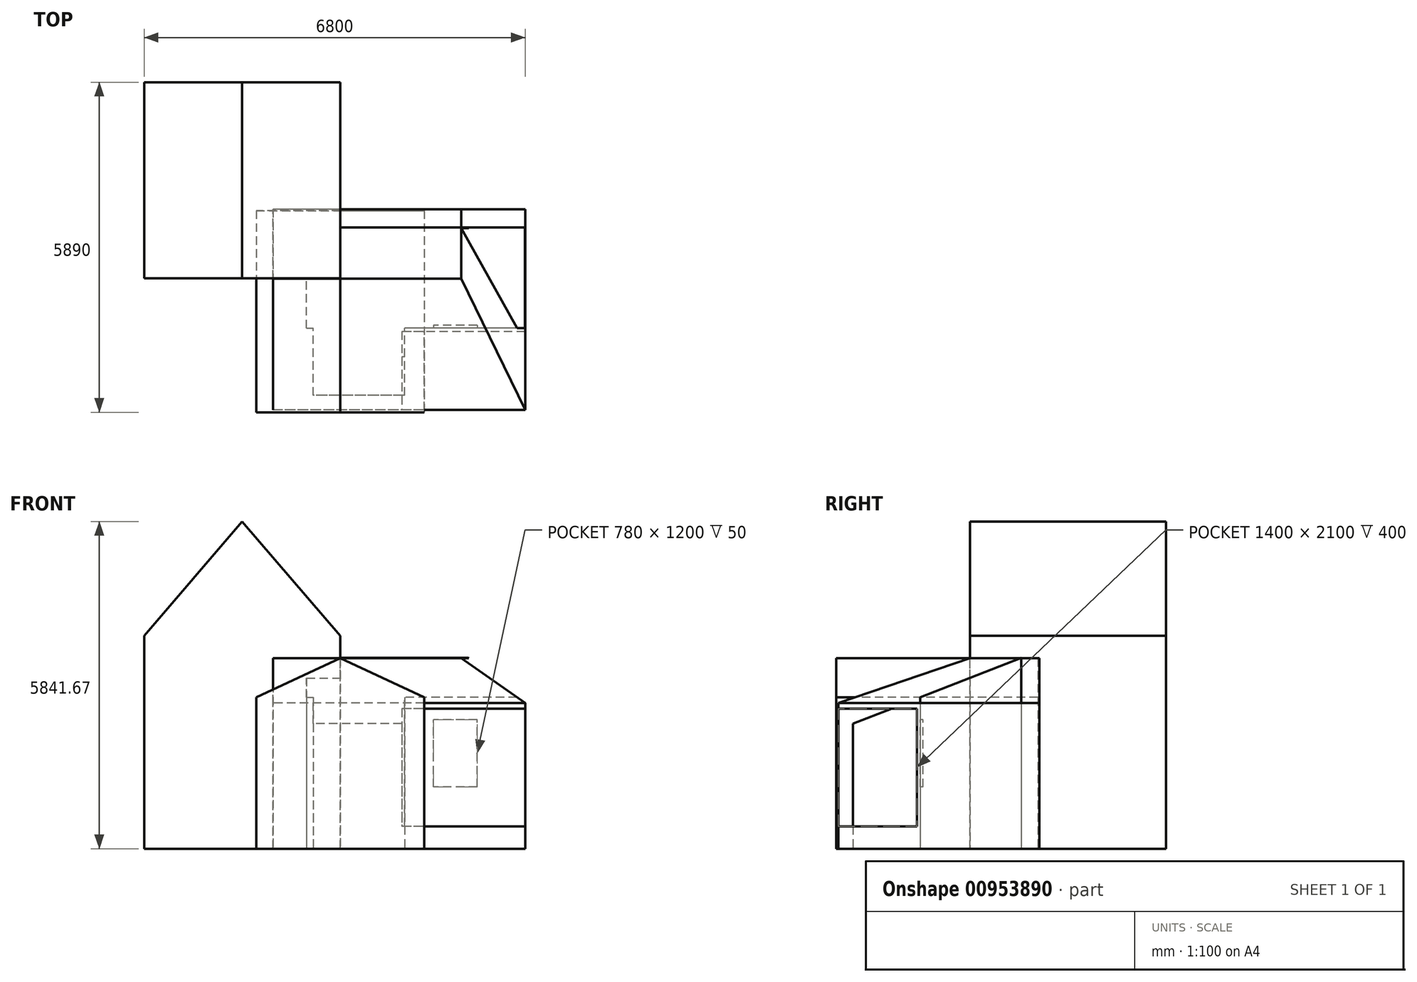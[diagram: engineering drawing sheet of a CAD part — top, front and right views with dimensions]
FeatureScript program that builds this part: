
annotation { "Feature Type Name" : "Feature", "Feature Type Description" : "" }
export const myFeature = defineFeature(function(context is Context, id is Id, definition is map)
    precondition{}
    {
        {
            var Q0;
            Q0=qCreatedBy(makeId("Right.planeOp"),FACE);
            var sketch = newSketch(context, id + "F0", { "sketchPlane" : qUnion([Q0])});
            skLineSegment(sketch, "E0", {"start": v(0, 0) * mm, "end": v(0, 2700) * mm});
            skLineSegment(sketch, "E1", {"start": v(1800, 0) * mm, "end": v(-1200, 0) * mm});
            skLineSegment(sketch, "E2", {"start": v(-1200, 0) * mm, "end": v(-1200, 2230) * mm});
            skLineSegment(sketch, "E3", {"start": v(-1200, 2230) * mm, "end": v(1800, 3405) * mm});
            skLineSegment(sketch, "E4", {"start": v(1800, 3405) * mm, "end": v(1800, 0) * mm});
            skSolve(sketch);
        }
        {
            var Q0;
            Q0 = qSketchRegion(id + "F0", true);
            extrude(context, id + "F1", {"entities" : qUnion([Q0]), "depth" : 3895 * mm, "offsetDistance" : 25 * mm});
        }
        {
            var Q0;
            Q0=qCreatedBy(makeId("Top.planeOp"),FACE);
            var sketch = newSketch(context, id + "F2", { "sketchPlane" : qUnion([Q0])});
            skLineSegment(sketch, "E5.bottom", {"start": v(3895, -1200) * mm, "end": v(1750, -1200) * mm});
            skLineSegment(sketch, "E5.top", {"start": v(3895, 0) * mm, "end": v(1750, 0) * mm});
            skLineSegment(sketch, "E5.left", {"start": v(3895, -1200) * mm, "end": v(3895, 0) * mm});
            skLineSegment(sketch, "E5.right", {"start": v(1750, -1200) * mm, "end": v(1750, 0) * mm});
            skLineSegment(sketch, "E6.bottom", {"start": v(0, -1200) * mm, "end": v(120, -1200) * mm});
            skLineSegment(sketch, "E6.top", {"start": v(0, 0) * mm, "end": v(120, 0) * mm});
            skLineSegment(sketch, "E6.left", {"start": v(0, -1200) * mm, "end": v(0, 0) * mm});
            skLineSegment(sketch, "E6.right", {"start": v(120, -1200) * mm, "end": v(120, 0) * mm});
            skSolve(sketch);
        }
        {
            var Q0;
            Q0 = qSketchRegion(id + "F2", true);
            var Q1;
            Q1=makeQuery(id+"F1.opExtrude","SWEPT_FACE",FACE,{"disambiguationData":[OSD([sQuery(id+"F0.wireOp",EDGE,"E3")])]});
            extrude(context, id + "F3", {"entities" : qUnion([Q0]), "operationType" : NewBodyOperationType.REMOVE, "endBound" : BoundingType.UP_TO_SURFACE, "depth" : 25 * mm, "endBoundEntityFace" : qUnion([Q1]), "offsetDistance" : 25 * mm});
        }
        {
            var Q0;
            Q0=qCreatedBy(makeId("Front.planeOp"),FACE);
            cPlane(context, id + "F4", {"entities" : qUnion([Q0]), "cplaneType" : CPlaneType.OFFSET, "offset" : 890 * mm, "oppositeDirection" : true, "width" : 150 * mm, "height" : 150 * mm});
        }
        {
            var Q0;
            Q0=qCreatedBy(id+"F4.planeOp",FACE);
            var sketch = newSketch(context, id + "F5", { "sketchPlane" : qUnion([Q0])});
            skLineSegment(sketch, "E7", {"start": v(600, 0) * mm, "end": v(-2900, 0) * mm});
            skLineSegment(sketch, "E8", {"start": v(-1150, 0) * mm, "end": v(-1150, 5841.67) * mm, "construction": true});
            skLineSegment(sketch, "E9", {"start": v(600, 0) * mm, "end": v(600, 3800) * mm});
            skLineSegment(sketch, "E10", {"start": v(600, 3800) * mm, "end": v(-1150, 5841.67) * mm});
            skLineSegment(sketch, "E11", {"start": v(-2900, 0) * mm, "end": v(-2900, 3800) * mm});
            skLineSegment(sketch, "E12", {"start": v(-2900, 3800) * mm, "end": v(-1150, 5841.67) * mm});
            skLineSegment(sketch, "E13", {"start": v(0, 3413.24) * mm, "end": v(0, 4500) * mm, "construction": true});
            skSolve(sketch);
        }
        {
            var Q0;
            Q0 = qSketchRegion(id + "F5", true);
            extrude(context, id + "F6", {"entities" : qUnion([Q0]), "operationType" : NewBodyOperationType.ADD, "oppositeDirection" : true, "depth" : 3500 * mm, "offsetDistance" : 25 * mm});
        }
        {
            var Q0;
            Q0=makeQuery(id+"F3.boolean.opBoolean","COPY",FACE,{"derivedFrom":makeQuery(id+"F3.opExtrude","SWEPT_FACE",FACE,{"disambiguationData":[OSD([sQuery(id+"F2.wireOp",EDGE,"E5.top")])]})});
            var sketch = newSketch(context, id + "F7", { "sketchPlane" : qUnion([Q0])});
            skLineSegment(sketch, "E14.bottom", {"start": v(3045, 1100) * mm, "end": v(2265, 1100) * mm});
            skLineSegment(sketch, "E14.top", {"start": v(3045, 2300) * mm, "end": v(2265, 2300) * mm});
            skLineSegment(sketch, "E14.left", {"start": v(3045, 1100) * mm, "end": v(3045, 2300) * mm});
            skLineSegment(sketch, "E14.right", {"start": v(2265, 1100) * mm, "end": v(2265, 2300) * mm});
            skSolve(sketch);
        }
        {
            var Q0;
            Q0=makeQuery(id+"F7.imprint","IMPRINT",FACE,{"disambiguationData":[TD([[makeQuery(id+"F7.imprint","IMPRINT",EDGE,{"derivedFrom":sQuery(id+"F7.wireOp",EDGE,"E14.bottom")}),-1.0]])]});
            extrude(context, id + "F8", {"entities" : qUnion([Q0]), "operationType" : NewBodyOperationType.REMOVE, "oppositeDirection" : true, "depth" : 50 * mm, "offsetDistance" : 25 * mm});
        }
        {
            var Q0;
            Q0=makeQuery(id+"F3.boolean.opBoolean","COPY",FACE,{"derivedFrom":makeQuery(id+"F3.opExtrude","SWEPT_FACE",FACE,{"disambiguationData":[OSD([sQuery(id+"F2.wireOp",EDGE,"E5.top")])]})});
            var sketch = newSketch(context, id + "F9", { "sketchPlane" : qUnion([Q0])});
            skLineSegment(sketch, "E15", {"start": v(3895, 2700) * mm, "end": v(3895, 3405) * mm});
            skLineSegment(sketch, "E16", {"start": v(3895, 3405) * mm, "end": v(2888.16, 3405) * mm});
            skLineSegment(sketch, "E17", {"start": v(2888.16, 3405) * mm, "end": v(3895, 2700) * mm});
            skSolve(sketch);
        }
        {
            var Q0;
            Q0=makeQuery(id+"F9.imprint","IMPRINT",FACE,{"disambiguationData":[TD([[makeQuery(id+"F9.imprint","IMPRINT",EDGE,{"derivedFrom":sQuery(id+"F9.wireOp",EDGE,"E15")}),1.0]])]});
            extrude(context, id + "F10", {"entities" : qUnion([Q0]), "operationType" : NewBodyOperationType.REMOVE, "oppositeDirection" : true, "depth" : 2190 * mm, "offsetDistance" : 25 * mm});
        }
        {
            var Q0;
            Q0=makeQuery(id+"F3.boolean.opBoolean","COPY",FACE,{"derivedFrom":makeQuery(id+"F3.opExtrude","SWEPT_FACE",FACE,{"disambiguationData":[OSD([sQuery(id+"F2.wireOp",EDGE,"E5.top")])]})});
            cPlane(context, id + "F11", {"entities" : qUnion([Q0]), "cplaneType" : CPlaneType.OFFSET, "offset" : 1500 * mm, "width" : 150 * mm, "height" : 150 * mm});
        }
        {
            var Q0;
            Q0=qCreatedBy(id+"F11.planeOp",FACE);
            var sketch = newSketch(context, id + "F12", { "sketchPlane" : qUnion([Q0])});
            skLineSegment(sketch, "E18", {"start": v(600, 3780.9) * mm, "end": v(600, 0) * mm, "construction": true});
            skLineSegment(sketch, "E19", {"start": v(600, 3400) * mm, "end": v(2100, 2700) * mm});
            skLineSegment(sketch, "E20", {"start": v(2100, 2700) * mm, "end": v(2100, 0) * mm});
            skLineSegment(sketch, "E21", {"start": v(2100, 0) * mm, "end": v(600, 0) * mm});
            skLineSegment(sketch, "E22.MirrorCS", {"start": v(600, 3400) * mm, "end": v(-900, 2700) * mm});
            skLineSegment(sketch, "E23.MirrorCS", {"start": v(-900, 2700) * mm, "end": v(-900, 0) * mm});
            skLineSegment(sketch, "E24.MirrorCS", {"start": v(-900, 0) * mm, "end": v(600, 0) * mm});
            skSolve(sketch);
        }
        {
            var Q0;
            Q0 = qSketchRegion(id + "F12", true);
            extrude(context, id + "F13", {"entities" : qUnion([Q0]), "oppositeDirection" : true, "depth" : 3600 * mm, "offsetDistance" : 25 * mm});
        }
        {
            var Q0;
            Q0=makeQuery(id+"F6.opExtrude","SWEPT_FACE",FACE,{"disambiguationData":[OSD([sQuery(id+"F5.wireOp",EDGE,"E9")])]});
            cPlane(context, id + "F14", {"entities" : qUnion([Q0]), "cplaneType" : CPlaneType.OFFSET, "offset" : 1200 * mm, "oppositeDirection" : true, "width" : 150 * mm, "height" : 150 * mm});
        }
        {
            var Q0;
            Q0=qCreatedBy(id+"F14.planeOp",FACE);
            var sketch = newSketch(context, id + "F15", { "sketchPlane" : qUnion([Q0])});
            skLineSegment(sketch, "E25", {"start": v(886.87, 3400) * mm, "end": v(2125.28, 3400) * mm});
            skLineSegment(sketch, "E26", {"start": v(2125.28, 3400) * mm, "end": v(2125.28, 0) * mm});
            skLineSegment(sketch, "E27", {"start": v(2125.28, 0) * mm, "end": v(-1460, 0) * mm});
            skLineSegment(sketch, "E28", {"start": v(-1460, 0) * mm, "end": v(-1460, 2600) * mm});
            skLineSegment(sketch, "E29", {"start": v(-1460, 2600) * mm, "end": v(886.87, 3400) * mm});
            skSolve(sketch);
        }
        {
            var Q0;
            Q0 = qSketchRegion(id + "F15", true);
            extrude(context, id + "F16", {"entities" : qUnion([Q0]), "depth" : 4500 * mm, "offsetDistance" : 25 * mm});
        }
        {
            var Q0;
            Q0=makeQuery(id+"F16.opExtrude","SWEPT_FACE",FACE,{"disambiguationData":[OSD([sQuery(id+"F15.wireOp",EDGE,"E28")])]});
            var sketch = newSketch(context, id + "F17", { "sketchPlane" : qUnion([Q0])});
            skLineSegment(sketch, "E30", {"start": v(3900, 2600) * mm, "end": v(3900, 3400) * mm});
            skLineSegment(sketch, "E31", {"start": v(3900, 3400) * mm, "end": v(2757.48, 3400) * mm});
            skLineSegment(sketch, "E32", {"start": v(2757.48, 3400) * mm, "end": v(3900, 2600) * mm});
            skSolve(sketch);
        }
        {
            var Q0;
            Q0=makeQuery(id+"F17.imprint","IMPRINT",FACE,{"disambiguationData":[TD([[makeQuery(id+"F17.imprint","IMPRINT",EDGE,{"derivedFrom":sQuery(id+"F17.wireOp",EDGE,"E30")}),1.0]])]});
            extrude(context, id + "F18", {"entities" : qUnion([Q0]), "operationType" : NewBodyOperationType.REMOVE, "oppositeDirection" : true, "depth" : 4050 * mm, "offsetDistance" : 25 * mm});
        }
        {
            var Q0;
            Q0=makeQuery(id+"F16.opExtrude","SWEPT_FACE",FACE,{"disambiguationData":[OSD([sQuery(id+"F15.wireOp",EDGE,"E28")])]});
            var sketch = newSketch(context, id + "F19", { "sketchPlane" : qUnion([Q0])});
            skLineSegment(sketch, "E33.bottom", {"start": v(3900, 2500) * mm, "end": v(1700, 2500) * mm});
            skLineSegment(sketch, "E33.top", {"start": v(3900, 400) * mm, "end": v(1700, 400) * mm});
            skLineSegment(sketch, "E33.left", {"start": v(3900, 2500) * mm, "end": v(3900, 400) * mm});
            skLineSegment(sketch, "E33.right", {"start": v(1700, 2500) * mm, "end": v(1700, 400) * mm});
            skSolve(sketch);
        }
        {
            var Q0;
            Q0=makeQuery(id+"F19.imprint","IMPRINT",FACE,{"disambiguationData":[TD([[makeQuery(id+"F19.imprint","IMPRINT",EDGE,{"derivedFrom":sQuery(id+"F19.wireOp",EDGE,"E33.bottom")}),1.0]])]});
            extrude(context, id + "F20", {"entities" : qUnion([Q0]), "operationType" : NewBodyOperationType.REMOVE, "oppositeDirection" : true, "depth" : 1400 * mm, "offsetDistance" : 25 * mm});
        }
    });
